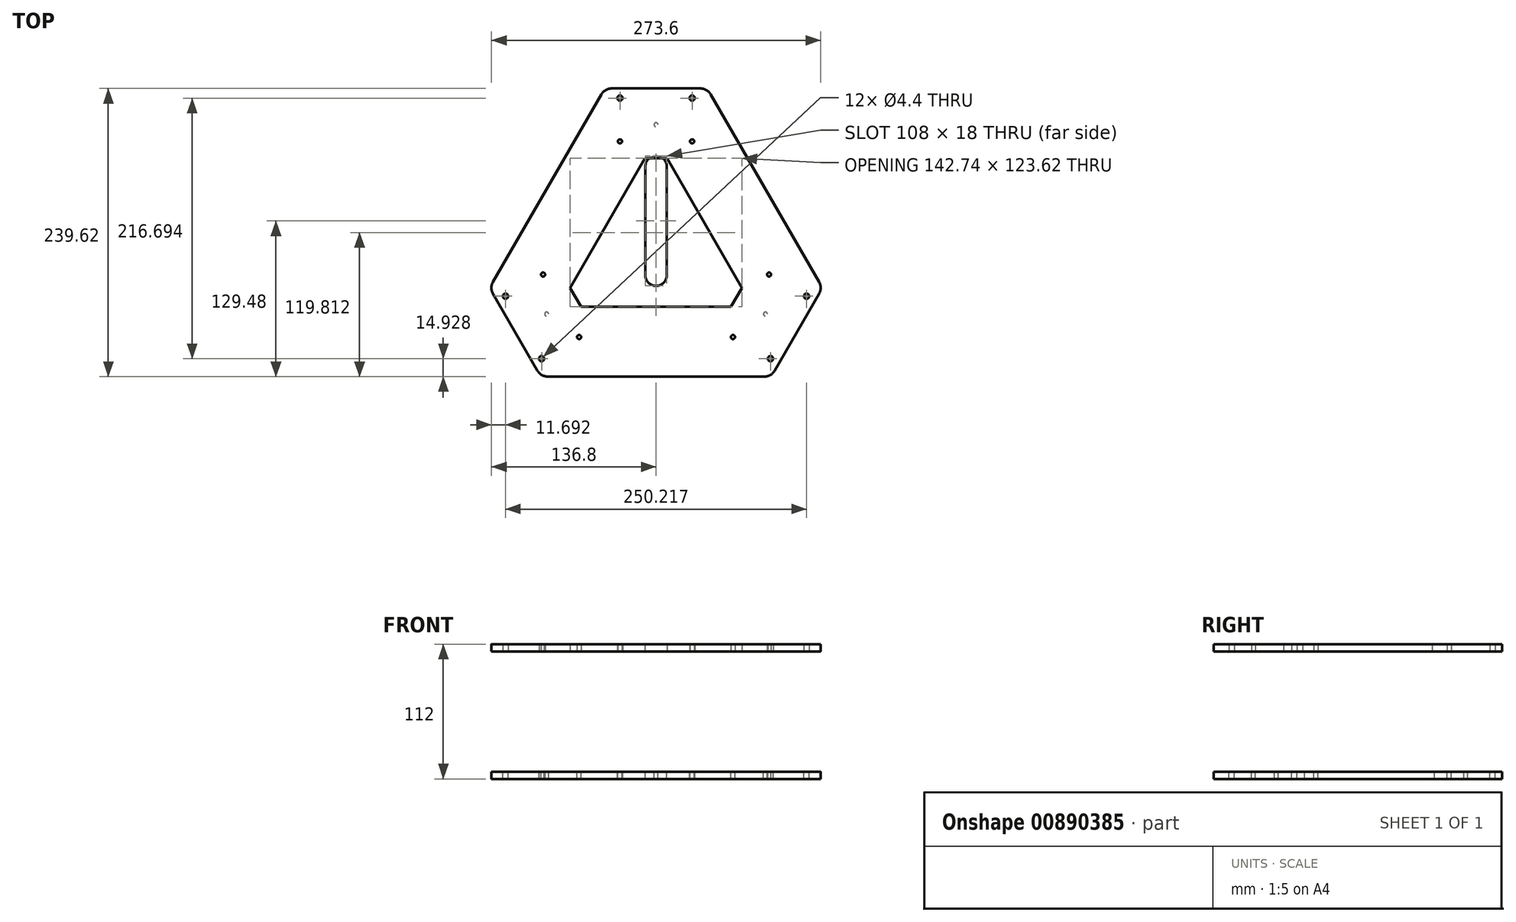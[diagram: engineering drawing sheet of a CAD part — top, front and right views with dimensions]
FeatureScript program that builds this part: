
annotation { "Feature Type Name" : "Feature", "Feature Type Description" : "" }
export const myFeature = defineFeature(function(context is Context, id is Id, definition is map)
    precondition{}
    {
        {
            var Q0;
            Q0=qCreatedBy(makeId("Top.planeOp"),FACE);
            var sketch = newSketch(context, id + "F0", { "sketchPlane" : qUnion([Q0])});
            skLineSegment(sketch, "E0", {"start": v(-138.34, -30.66) * mm, "end": v(-42.62, 135.14) * mm});
            skLineSegment(sketch, "E1", {"start": v(-42.62, 135.14) * mm, "end": v(42.62, 135.14) * mm});
            skLineSegment(sketch, "E2", {"start": v(42.62, 135.14) * mm, "end": v(138.34, -30.66) * mm});
            skLineSegment(sketch, "E3", {"start": v(138.34, -30.66) * mm, "end": v(95.73, -104.48) * mm});
            skLineSegment(sketch, "E4", {"start": v(95.73, -104.48) * mm, "end": v(-95.73, -104.48) * mm});
            skLineSegment(sketch, "E5", {"start": v(-95.73, -104.48) * mm, "end": v(-138.34, -30.66) * mm});
            skLineSegment(sketch, "E6", {"start": v(-90.48, 52.24) * mm, "end": v(0, 0) * mm, "construction": true});
            skLineSegment(sketch, "E7", {"start": v(0, -104.48) * mm, "end": v(0, 0) * mm, "construction": true});
            skLineSegment(sketch, "E8", {"start": v(90.48, 52.24) * mm, "end": v(0, 0) * mm, "construction": true});
            skPoint(sketch, "E9", {"position": v(0, 0) * mm});
            skLineSegment(sketch, "E10.0", {"start": v(62.24, -46.48) * mm, "end": v(-62.24, -46.48) * mm});
            skLineSegment(sketch, "E10.1", {"start": v(-71.37, -30.66) * mm, "end": v(-9.13, 77.14) * mm});
            skLineSegment(sketch, "E10.2", {"start": v(-9.13, 77.14) * mm, "end": v(9.13, 77.14) * mm});
            skLineSegment(sketch, "E10.3", {"start": v(-62.24, -46.48) * mm, "end": v(-71.37, -30.66) * mm});
            skLineSegment(sketch, "E10.4", {"start": v(9.13, 77.14) * mm, "end": v(71.37, -30.66) * mm});
            skLineSegment(sketch, "E10.5", {"start": v(71.37, -30.66) * mm, "end": v(62.24, -46.48) * mm});
            skCircle(sketch, "E11", {"center": v(95.1, -89.55) * mm, "radius": 2.2 * mm});
            skLineSegment(sketch, "E12", {"start": v(117.04, -67.57) * mm, "end": v(66.8, -38.57) * mm, "construction": true});
            skCircle(sketch, "E13", {"center": v(63.93, -71.55) * mm, "radius": 1.7 * mm});
            skCircle(sketch, "E14.MirrorC", {"center": v(93.93, -19.6) * mm, "radius": 1.7 * mm});
            skCircle(sketch, "E15.MirrorC", {"center": v(125.1, -37.6) * mm, "radius": 2.2 * mm});
            skPoint(sketch, "E16.center", {"position": v(-138.34, -30.66) * mm});
            skLineSegment(sketch, "E17.0", {"start": v(95.1, -89.55) * mm, "end": v(95.1, -89.55) * mm});
            skLineSegment(sketch, "E17.1", {"start": v(95.1, -89.55) * mm, "end": v(63.93, -71.55) * mm, "construction": true});
            skCircle(sketch, "E18.1.0", {"center": v(30, 91.14) * mm, "radius": 1.7 * mm});
            skCircle(sketch, "E18.1.1", {"center": v(30, 127.14) * mm, "radius": 2.2 * mm});
            skCircle(sketch, "E18.1.2", {"center": v(-30, 127.14) * mm, "radius": 2.2 * mm});
            skCircle(sketch, "E18.1.3", {"center": v(-30, 91.14) * mm, "radius": 1.7 * mm});
            skCircle(sketch, "E18.2.0", {"center": v(-93.93, -19.6) * mm, "radius": 1.7 * mm});
            skCircle(sketch, "E18.2.1", {"center": v(-125.1, -37.6) * mm, "radius": 2.2 * mm});
            skCircle(sketch, "E18.2.2", {"center": v(-95.1, -89.55) * mm, "radius": 2.2 * mm});
            skCircle(sketch, "E18.2.3", {"center": v(-63.93, -71.55) * mm, "radius": 1.7 * mm});
            skSolve(sketch);
        }
        {
            var Q0;
            {var subQ0=sQuery(id+"F0.wireOp",EDGE,"vAaXFV3b-EpbO-ac0L-dCJ6-TkjUisyF59UN");Q0=makeQuery(id+"F0.imprint","IMPRINT",FACE,{"disambiguationData":[TD([[makeQuery(id+"F0.imprint","IMPRINT",EDGE,{"derivedFrom":subQ0}),1.0]])]});}
            var Q1;
            Q1=makeQuery(id+"F0.imprint","IMPRINT",FACE,{"disambiguationData":[TD([[makeQuery(id+"F0.imprint","IMPRINT",EDGE,{"derivedFrom":sQuery(id+"F0.wireOp",EDGE,"E0")}),-1.0]])]});
            extrude(context, id + "F1", {"entities" : qUnion([Q0, Q1]), "depth" : 6 * mm, "offsetDistance" : 25 * mm});
        }
        {
            var Q0;
            Q0=makeQuery(id+"F1.opExtrude","CAP_FACE",FACE,{"disambiguationData":[OSD([sQuery(id+"F0.wireOp",EDGE,"E0"),sQuery(id+"F0.wireOp",EDGE,"E1"),sQuery(id+"F0.wireOp",EDGE,"E2"),sQuery(id+"F0.wireOp",EDGE,"E3"),sQuery(id+"F0.wireOp",EDGE,"E4"),sQuery(id+"F0.wireOp",EDGE,"E5"),sQuery(id+"F0.wireOp",EDGE,"E10.0"),sQuery(id+"F0.wireOp",EDGE,"E10.1"),sQuery(id+"F0.wireOp",EDGE,"E10.2"),sQuery(id+"F0.wireOp",EDGE,"E10.3"),sQuery(id+"F0.wireOp",EDGE,"E10.4"),sQuery(id+"F0.wireOp",EDGE,"E10.5")])],"isStart":true});
            cPlane(context, id + "F2", {"entities" : qUnion([Q0]), "cplaneType" : CPlaneType.OFFSET, "offset" : 100 * mm, "width" : 150 * mm, "height" : 150 * mm});
        }
        {
            var Q0;
            Q0=qCreatedBy(id+"F2.planeOp",FACE);
            var sketch = newSketch(context, id + "F3", { "sketchPlane" : qUnion([Q0])});
            skLineSegment(sketch, "E19", {"start": v(-95.73, 104.48) * mm, "end": v(95.73, 104.48) * mm});
            skLineSegment(sketch, "E20", {"start": v(95.73, 104.48) * mm, "end": v(138.34, 30.66) * mm});
            skLineSegment(sketch, "E21", {"start": v(138.34, 30.66) * mm, "end": v(42.62, -135.14) * mm});
            skLineSegment(sketch, "E22", {"start": v(42.62, -135.14) * mm, "end": v(-42.62, -135.14) * mm});
            skLineSegment(sketch, "E23", {"start": v(-42.62, -135.14) * mm, "end": v(-138.34, 30.66) * mm});
            skLineSegment(sketch, "E24", {"start": v(-138.34, 30.66) * mm, "end": v(-95.73, 104.48) * mm});
            skLineSegment(sketch, "E25", {"start": v(-90.48, -52.24) * mm, "end": v(0, 0) * mm, "construction": true});
            skLineSegment(sketch, "E26", {"start": v(90.48, -52.24) * mm, "end": v(0, 0) * mm, "construction": true});
            skLineSegment(sketch, "E27", {"start": v(0, 104.48) * mm, "end": v(0, 0) * mm, "construction": true});
            skCircle(sketch, "E28", {"center": v(0, 0) * mm, "radius": 110 * mm, "construction": true});
            skCircle(sketch, "E29", {"center": v(0, -105) * mm, "radius": 1.65 * mm});
            skLineSegment(sketch, "E30", {"start": v(0, 20) * mm, "end": v(0, -70) * mm, "construction": true});
            skArc(sketch, "E31.0.startCap", {"start": v(-9, 20) * mm, "mid": v(0, 29) * mm, "end": v(9, 20) * mm});
            skArc(sketch, "E31.0.endCap", {"start": v(9, -70) * mm, "mid": v(0, -79) * mm, "end": v(-9, -70) * mm});
            skLineSegment(sketch, "E31.0.left", {"start": v(9, 20) * mm, "end": v(9, -70) * mm});
            skLineSegment(sketch, "E31.0.right", {"start": v(-9, 20) * mm, "end": v(-9, -70) * mm});
            skCircle(sketch, "E32.1.0", {"center": v(90.93, 52.5) * mm, "radius": 1.65 * mm});
            skCircle(sketch, "E32.2.0", {"center": v(-90.93, 52.5) * mm, "radius": 1.65 * mm});
            skCircle(sketch, "E33", {"center": v(95.1, 89.55) * mm, "radius": 2.2 * mm});
            skCircle(sketch, "E34", {"center": v(63.93, 71.55) * mm, "radius": 1.7 * mm});
            skLineSegment(sketch, "E35", {"start": v(117.04, 67.57) * mm, "end": v(66.8, 38.57) * mm, "construction": true});
            skCircle(sketch, "E36.MirrorC", {"center": v(93.93, 19.6) * mm, "radius": 1.7 * mm});
            skCircle(sketch, "E37.MirrorC", {"center": v(125.1, 37.6) * mm, "radius": 2.2 * mm});
            skCircle(sketch, "E38.1.0", {"center": v(-93.93, 19.6) * mm, "radius": 1.7 * mm});
            skCircle(sketch, "E38.1.1", {"center": v(-125.1, 37.6) * mm, "radius": 2.2 * mm});
            skCircle(sketch, "E38.1.2", {"center": v(-95.1, 89.55) * mm, "radius": 2.2 * mm});
            skCircle(sketch, "E38.1.3", {"center": v(-63.93, 71.55) * mm, "radius": 1.7 * mm});
            skCircle(sketch, "E38.2.0", {"center": v(30, -91.14) * mm, "radius": 1.7 * mm});
            skCircle(sketch, "E38.2.1", {"center": v(30, -127.14) * mm, "radius": 2.2 * mm});
            skCircle(sketch, "E38.2.2", {"center": v(-30, -127.14) * mm, "radius": 2.2 * mm});
            skCircle(sketch, "E38.2.3", {"center": v(-30, -91.14) * mm, "radius": 1.7 * mm});
            skSolve(sketch);
        }
        {
            var Q0;
            Q0 = qSketchRegion(id + "F3", true);
            extrude(context, id + "F4", {"entities" : qUnion([Q0]), "depth" : 6 * mm, "offsetDistance" : 25 * mm});
        }
        {
            var Q0;
            Q0=makeQuery(id+"F1.opExtrude","SWEPT_EDGE",EDGE,{"disambiguationData":[OSD([sQuery(id+"F0.wireOp",EDGE,"E3"),sQuery(id+"F0.wireOp",EDGE,"E4")])]});
            var Q1;
            Q1=makeQuery(id+"F1.opExtrude","SWEPT_EDGE",EDGE,{"disambiguationData":[OSD([sQuery(id+"F0.wireOp",EDGE,"E2"),sQuery(id+"F0.wireOp",EDGE,"E3")])]});
            var Q2;
            Q2=makeQuery(id+"F1.opExtrude","SWEPT_EDGE",EDGE,{"disambiguationData":[OSD([sQuery(id+"F0.wireOp",EDGE,"E4"),sQuery(id+"F0.wireOp",EDGE,"E5")])]});
            var Q3;
            Q3=makeQuery(id+"F1.opExtrude","SWEPT_EDGE",EDGE,{"disambiguationData":[OSD([sQuery(id+"F0.wireOp",EDGE,"E0"),sQuery(id+"F0.wireOp",EDGE,"E5")])]});
            var Q4;
            Q4=makeQuery(id+"F1.opExtrude","SWEPT_EDGE",EDGE,{"disambiguationData":[OSD([sQuery(id+"F0.wireOp",EDGE,"E0"),sQuery(id+"F0.wireOp",EDGE,"E1")])]});
            var Q5;
            Q5=makeQuery(id+"F1.opExtrude","SWEPT_EDGE",EDGE,{"disambiguationData":[OSD([sQuery(id+"F0.wireOp",EDGE,"E1"),sQuery(id+"F0.wireOp",EDGE,"E2")])]});
            var Q6;
            Q6=makeQuery(id+"F4.opExtrude","SWEPT_EDGE",EDGE,{"disambiguationData":[OSD([sQuery(id+"F3.wireOp",EDGE,"E22"),sQuery(id+"F3.wireOp",EDGE,"E23")])]});
            var Q7;
            Q7=makeQuery(id+"F4.opExtrude","SWEPT_EDGE",EDGE,{"disambiguationData":[OSD([sQuery(id+"F3.wireOp",EDGE,"E21"),sQuery(id+"F3.wireOp",EDGE,"E22")])]});
            var Q8;
            Q8=makeQuery(id+"F4.opExtrude","SWEPT_EDGE",EDGE,{"disambiguationData":[OSD([sQuery(id+"F3.wireOp",EDGE,"E20"),sQuery(id+"F3.wireOp",EDGE,"E21")])]});
            var Q9;
            Q9=makeQuery(id+"F4.opExtrude","SWEPT_EDGE",EDGE,{"disambiguationData":[OSD([sQuery(id+"F3.wireOp",EDGE,"E19"),sQuery(id+"F3.wireOp",EDGE,"E20")])]});
            var Q10;
            Q10=makeQuery(id+"F4.opExtrude","SWEPT_EDGE",EDGE,{"disambiguationData":[OSD([sQuery(id+"F3.wireOp",EDGE,"E19"),sQuery(id+"F3.wireOp",EDGE,"E24")])]});
            var Q11;
            Q11=makeQuery(id+"F4.opExtrude","SWEPT_EDGE",EDGE,{"disambiguationData":[OSD([sQuery(id+"F3.wireOp",EDGE,"E23"),sQuery(id+"F3.wireOp",EDGE,"E24")])]});
            fillet(context, id + "F5", {"entities" : qUnion([Q0, Q1, Q2, Q3, Q4, Q5, Q6, Q7, Q8, Q9, Q10, Q11]), "radius" : 10 * mm, "tangentPropagation" : true, "allowEdgeOverflow" : false});
        }
    });
